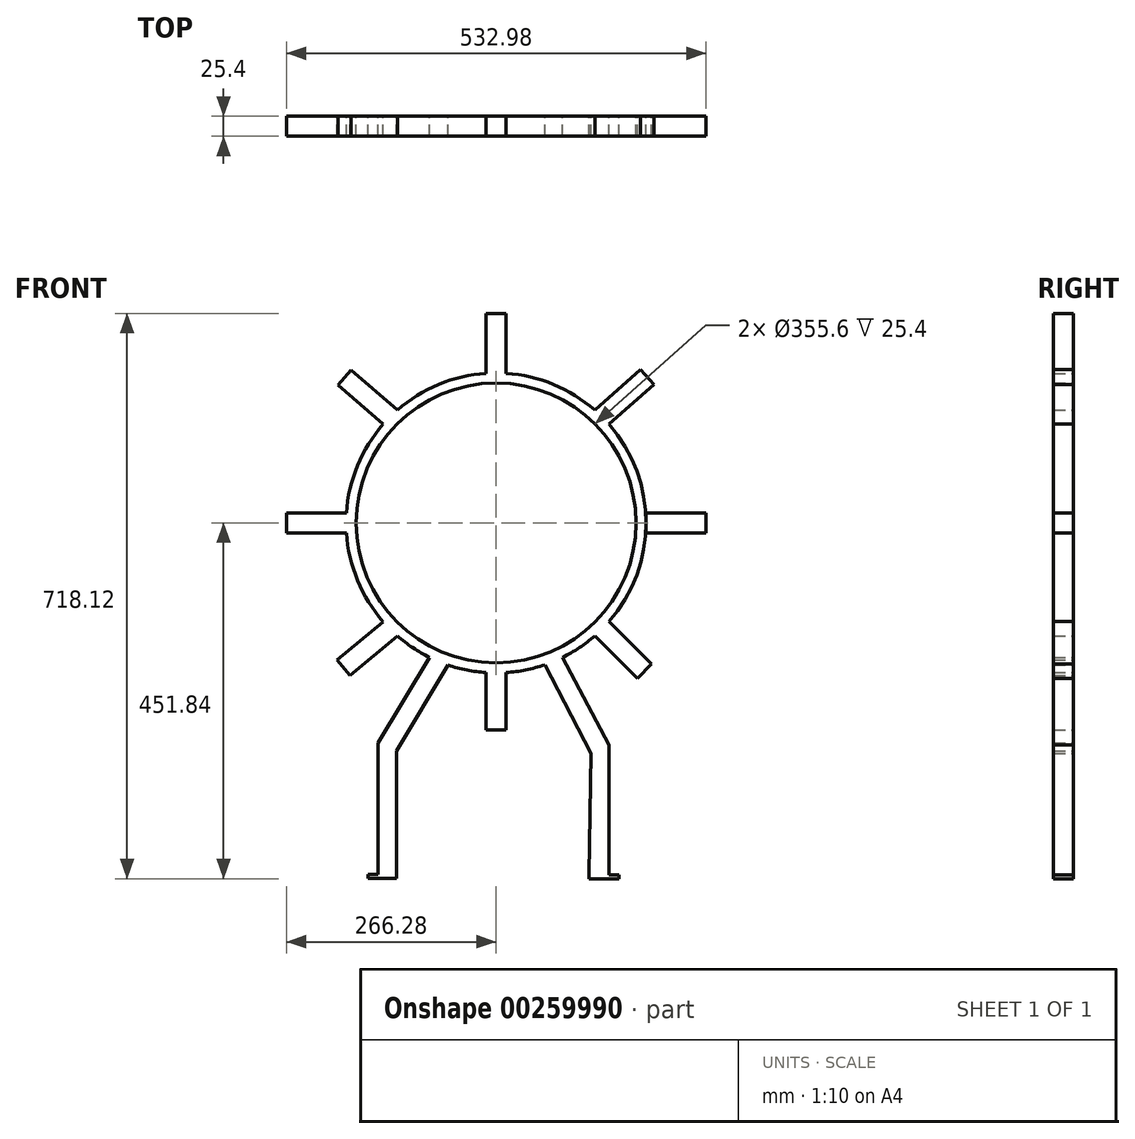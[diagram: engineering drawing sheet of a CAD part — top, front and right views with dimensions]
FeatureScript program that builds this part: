
annotation { "Feature Type Name" : "Feature", "Feature Type Description" : "" }
export const myFeature = defineFeature(function(context is Context, id is Id, definition is map)
    precondition{}
    {
        {
            var Q0;
            Q0=qCreatedBy(makeId("Front.planeOp"),FACE);
            var sketch = newSketch(context, id + "F0", { "sketchPlane" : qUnion([Q0])});
            skCircle(sketch, "E0", {"center": v(0, 0) * mm, "radius": 190.5 * mm});
            skCircle(sketch, "E1", {"center": v(0, 0) * mm, "radius": 177.8 * mm});
            skLineSegment(sketch, "E2", {"start": v(-190.08, 12.7) * mm, "end": v(-190.08, -12.7) * mm});
            skLineSegment(sketch, "E3", {"start": v(-190.08, -12.7) * mm, "end": v(-266.28, -12.7) * mm});
            skLineSegment(sketch, "E4", {"start": v(-266.28, -12.7) * mm, "end": v(-266.28, 12.7) * mm});
            skLineSegment(sketch, "E5", {"start": v(-266.28, 12.7) * mm, "end": v(-190.08, 12.7) * mm});
            skLineSegment(sketch, "E6", {"start": v(190.5, 12.7) * mm, "end": v(190.5, -12.7) * mm});
            skLineSegment(sketch, "E7", {"start": v(190.5, -12.7) * mm, "end": v(266.7, -12.7) * mm});
            skLineSegment(sketch, "E8", {"start": v(266.7, -12.7) * mm, "end": v(266.7, 12.7) * mm});
            skLineSegment(sketch, "E9", {"start": v(266.7, 12.7) * mm, "end": v(190.5, 12.7) * mm});
            skLineSegment(sketch, "E10", {"start": v(-12.7, 190.08) * mm, "end": v(12.7, 190.08) * mm});
            skLineSegment(sketch, "E11", {"start": v(12.7, 190.08) * mm, "end": v(12.7, 266.28) * mm});
            skLineSegment(sketch, "E12", {"start": v(12.7, 266.28) * mm, "end": v(-12.7, 266.28) * mm});
            skLineSegment(sketch, "E13", {"start": v(-12.7, 266.28) * mm, "end": v(-12.7, 190.08) * mm});
            skLineSegment(sketch, "E14", {"start": v(-12.7, -190.08) * mm, "end": v(-12.7, -262.66) * mm});
            skLineSegment(sketch, "E15", {"start": v(-12.7, -262.66) * mm, "end": v(12.7, -262.8) * mm});
            skLineSegment(sketch, "E16", {"start": v(12.7, -262.8) * mm, "end": v(12.7, -186.6) * mm});
            skLineSegment(sketch, "E17", {"start": v(125.42, 143.38) * mm, "end": v(143.38, 125.43) * mm});
            skLineSegment(sketch, "E18", {"start": v(143.38, 125.43) * mm, "end": v(200.44, 175.93) * mm});
            skLineSegment(sketch, "E19", {"start": v(200.44, 175.93) * mm, "end": v(183.65, 194.9) * mm});
            skLineSegment(sketch, "E20", {"start": v(183.65, 194.9) * mm, "end": v(125.42, 143.38) * mm});
            skLineSegment(sketch, "E21", {"start": v(-143.38, -125.43) * mm, "end": v(-201.87, -174.26) * mm});
            skLineSegment(sketch, "E22", {"start": v(-201.87, -174.26) * mm, "end": v(-185.57, -193.74) * mm});
            skLineSegment(sketch, "E23", {"start": v(-185.57, -193.74) * mm, "end": v(-125.42, -143.38) * mm});
            skLineSegment(sketch, "E24", {"start": v(-143.38, 125.42) * mm, "end": v(-200.9, 175.4) * mm});
            skLineSegment(sketch, "E25", {"start": v(-200.9, 175.4) * mm, "end": v(-184.3, 194.52) * mm});
            skLineSegment(sketch, "E26", {"start": v(-184.3, 194.52) * mm, "end": v(-125.43, 143.38) * mm});
            skLineSegment(sketch, "E27", {"start": v(125.43, -143.38) * mm, "end": v(179.32, -197.25) * mm});
            skLineSegment(sketch, "E28", {"start": v(179.32, -197.25) * mm, "end": v(197.28, -179.3) * mm});
            skLineSegment(sketch, "E29", {"start": v(197.28, -179.3) * mm, "end": v(143.4, -125.41) * mm});
            skLineSegment(sketch, "E30", {"start": v(-12.7, -190.08) * mm, "end": v(-12.7, -177.35) * mm});
            skLineSegment(sketch, "E31", {"start": v(12.7, -186.6) * mm, "end": v(12.7, -177.35) * mm});
            skLineSegment(sketch, "E32", {"start": v(-84.42, -170.77) * mm, "end": v(-149.93, -279.57) * mm});
            skLineSegment(sketch, "E33", {"start": v(-149.93, -279.57) * mm, "end": v(-126.47, -289.29) * mm});
            skLineSegment(sketch, "E34", {"start": v(-126.47, -289.29) * mm, "end": v(-60.97, -180.48) * mm});
            skLineSegment(sketch, "E35", {"start": v(61.97, -180.14) * mm, "end": v(120.58, -292.8) * mm});
            skLineSegment(sketch, "E36", {"start": v(84.45, -170.76) * mm, "end": v(143.47, -281.8) * mm});
            skLineSegment(sketch, "E37", {"start": v(120.58, -292.8) * mm, "end": v(143.47, -281.8) * mm});
            skLineSegment(sketch, "E38", {"start": v(-149.93, -279.57) * mm, "end": v(-149.93, -446.34) * mm});
            skLineSegment(sketch, "E39", {"start": v(-149.93, -446.34) * mm, "end": v(-126.47, -446.34) * mm});
            skLineSegment(sketch, "E40", {"start": v(-126.47, -446.34) * mm, "end": v(-126.47, -289.29) * mm});
            skLineSegment(sketch, "E41", {"start": v(120.58, -292.8) * mm, "end": v(118.07, -446.34) * mm});
            skLineSegment(sketch, "E42", {"start": v(118.07, -446.34) * mm, "end": v(143.47, -446.76) * mm});
            skLineSegment(sketch, "E43", {"start": v(143.47, -446.76) * mm, "end": v(143.47, -281.8) * mm});
            skLineSegment(sketch, "E44", {"start": v(143.47, -446.76) * mm, "end": v(156.17, -446.76) * mm});
            skLineSegment(sketch, "E45", {"start": v(156.17, -446.76) * mm, "end": v(156.17, -451.84) * mm});
            skLineSegment(sketch, "E46", {"start": v(156.17, -451.84) * mm, "end": v(117.92, -451.84) * mm});
            skLineSegment(sketch, "E47", {"start": v(117.92, -451.84) * mm, "end": v(118.07, -446.34) * mm});
            skLineSegment(sketch, "E48", {"start": v(-149.93, -446.34) * mm, "end": v(-149.93, -451.42) * mm});
            skLineSegment(sketch, "E49", {"start": v(-149.93, -451.42) * mm, "end": v(-126.46, -451.42) * mm});
            skLineSegment(sketch, "E50", {"start": v(-126.46, -451.42) * mm, "end": v(-126.47, -446.34) * mm});
            skLineSegment(sketch, "E51", {"start": v(-149.93, -446.34) * mm, "end": v(-162.63, -446.34) * mm});
            skLineSegment(sketch, "E52", {"start": v(-162.63, -446.34) * mm, "end": v(-162.63, -451.42) * mm});
            skLineSegment(sketch, "E53", {"start": v(-162.63, -451.42) * mm, "end": v(-149.93, -451.42) * mm});
            skSolve(sketch);
        }
        {
            var Q0;
            Q0 = qSketchRegion(id + "F0", true);
            extrude(context, id + "F1", {"entities" : qUnion([Q0]), "endBound" : BoundingType.SYMMETRIC, "depth" : 25.4 * mm});
        }
    });
